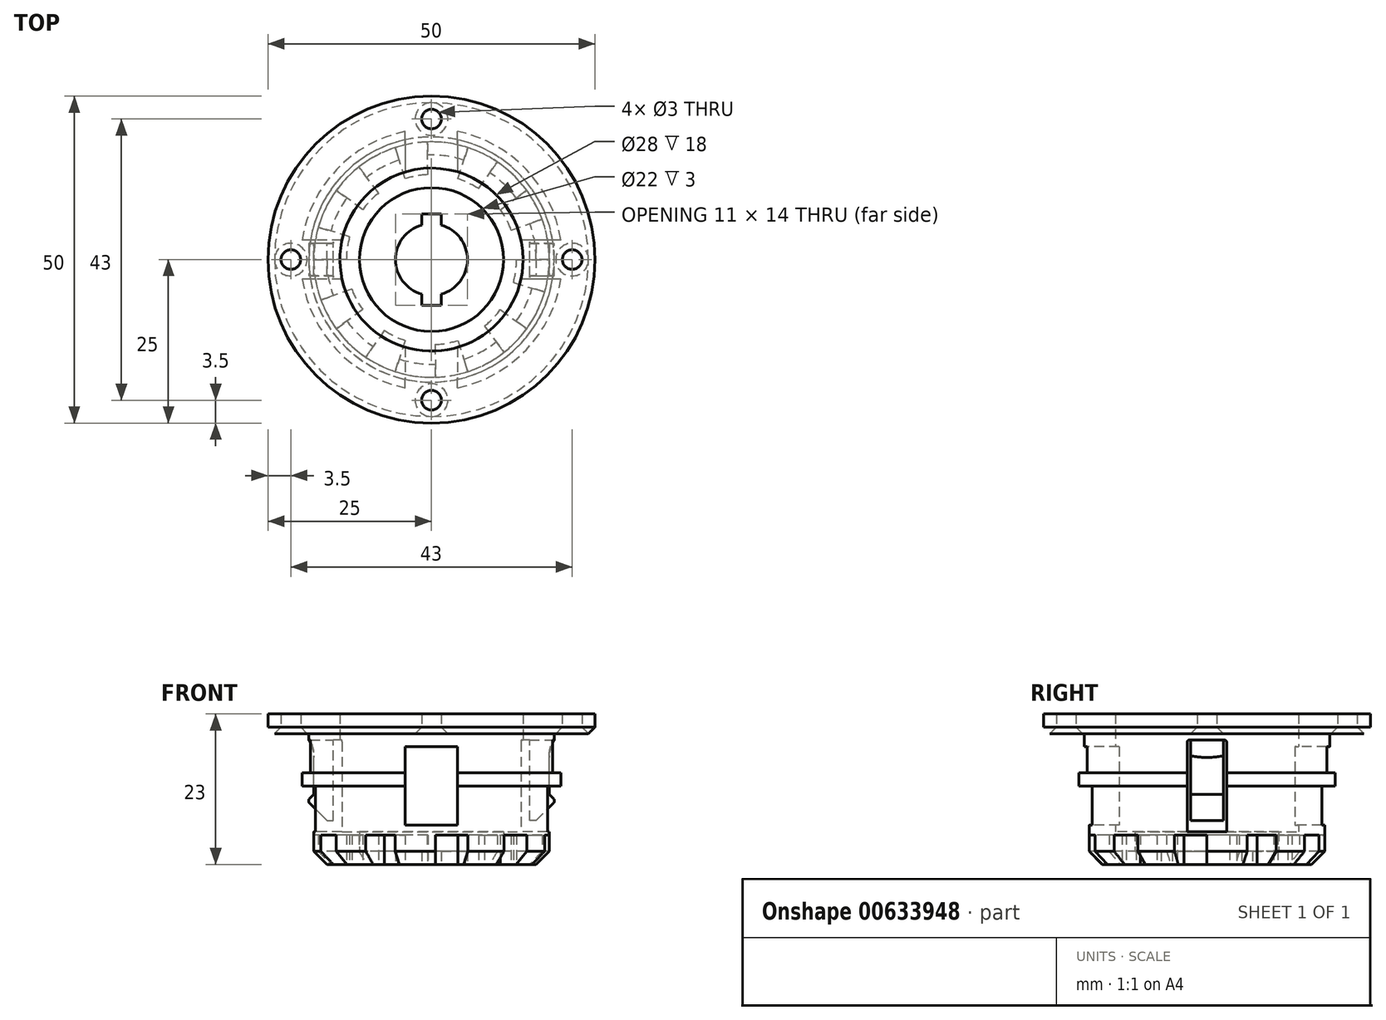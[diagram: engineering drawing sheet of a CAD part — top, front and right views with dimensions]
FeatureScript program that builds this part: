
annotation { "Feature Type Name" : "Feature", "Feature Type Description" : "" }
export const myFeature = defineFeature(function(context is Context, id is Id, definition is map)
    precondition{}
    {
        {
            var Q0;
            Q0=qCreatedBy(makeId("Top.planeOp"),FACE);
            var sketch = newSketch(context, id + "F0", { "sketchPlane" : qUnion([Q0])});
            skArc(sketch, "E0", {"start": v(18, 0) * mm, "mid": v(17.83, -2.5) * mm, "end": v(17.3, -4.95) * mm});
            skArc(sketch, "E1", {"start": v(13, 0) * mm, "mid": v(12.88, -1.77) * mm, "end": v(12.52, -3.5) * mm});
            skLineSegment(sketch, "E2", {"start": v(13, 0) * mm, "end": v(18, 0) * mm});
            skLineSegment(sketch, "E3", {"start": v(12.52, -3.5) * mm, "end": v(17.3, -4.95) * mm});
            skArc(sketch, "E4.1.0", {"start": v(10.52, -7.64) * mm, "mid": v(9.38, -9) * mm, "end": v(8.07, -10.2) * mm});
            skArc(sketch, "E4.1.1", {"start": v(14.56, -10.58) * mm, "mid": v(12.95, -12.5) * mm, "end": v(11.1, -14.18) * mm});
            skLineSegment(sketch, "E4.1.2", {"start": v(10.52, -7.64) * mm, "end": v(14.56, -10.58) * mm});
            skLineSegment(sketch, "E4.1.3", {"start": v(8.07, -10.2) * mm, "end": v(11.1, -14.18) * mm});
            skArc(sketch, "E4.2.0", {"start": v(4.02, -12.36) * mm, "mid": v(2.3, -12.8) * mm, "end": v(0.54, -12.99) * mm});
            skArc(sketch, "E4.2.1", {"start": v(5.56, -17.12) * mm, "mid": v(3.13, -17.73) * mm, "end": v(0.64, -17.99) * mm});
            skLineSegment(sketch, "E4.2.2", {"start": v(4.02, -12.36) * mm, "end": v(5.56, -17.12) * mm});
            skLineSegment(sketch, "E4.2.3", {"start": v(0.54, -12.99) * mm, "end": v(0.64, -17.99) * mm});
            skArc(sketch, "E4.3.0", {"start": v(-4.02, -12.36) * mm, "mid": v(-5.66, -11.7) * mm, "end": v(-7.2, -10.83) * mm});
            skArc(sketch, "E4.3.1", {"start": v(-5.56, -17.12) * mm, "mid": v(-7.89, -16.18) * mm, "end": v(-10.06, -14.93) * mm});
            skLineSegment(sketch, "E4.3.2", {"start": v(-4.02, -12.36) * mm, "end": v(-5.56, -17.12) * mm});
            skLineSegment(sketch, "E4.3.3", {"start": v(-7.2, -10.83) * mm, "end": v(-10.06, -14.93) * mm});
            skArc(sketch, "E4.4.0", {"start": v(-10.52, -7.64) * mm, "mid": v(-11.46, -6.14) * mm, "end": v(-12.19, -4.53) * mm});
            skArc(sketch, "E4.4.1", {"start": v(-14.56, -10.58) * mm, "mid": v(-15.9, -8.46) * mm, "end": v(-16.91, -6.17) * mm});
            skLineSegment(sketch, "E4.4.2", {"start": v(-10.52, -7.64) * mm, "end": v(-14.56, -10.58) * mm});
            skLineSegment(sketch, "E4.4.3", {"start": v(-12.19, -4.53) * mm, "end": v(-16.91, -6.17) * mm});
            skArc(sketch, "E4.5.0", {"start": v(-13, 0) * mm, "mid": v(-12.88, 1.77) * mm, "end": v(-12.52, 3.5) * mm});
            skArc(sketch, "E4.5.1", {"start": v(-18, 0) * mm, "mid": v(-17.83, 2.5) * mm, "end": v(-17.3, 4.95) * mm});
            skLineSegment(sketch, "E4.5.2", {"start": v(-13, 0) * mm, "end": v(-18, 0) * mm});
            skLineSegment(sketch, "E4.5.3", {"start": v(-12.52, 3.5) * mm, "end": v(-17.3, 4.95) * mm});
            skArc(sketch, "E4.6.0", {"start": v(-10.52, 7.64) * mm, "mid": v(-9.38, 9) * mm, "end": v(-8.07, 10.2) * mm});
            skArc(sketch, "E4.6.1", {"start": v(-14.56, 10.58) * mm, "mid": v(-12.95, 12.5) * mm, "end": v(-11.1, 14.18) * mm});
            skLineSegment(sketch, "E4.6.2", {"start": v(-10.52, 7.64) * mm, "end": v(-14.56, 10.58) * mm});
            skLineSegment(sketch, "E4.6.3", {"start": v(-8.07, 10.2) * mm, "end": v(-11.1, 14.18) * mm});
            skArc(sketch, "E4.7.0", {"start": v(-4.02, 12.36) * mm, "mid": v(-2.3, 12.8) * mm, "end": v(-0.54, 12.99) * mm});
            skArc(sketch, "E4.7.1", {"start": v(-5.56, 17.12) * mm, "mid": v(-3.13, 17.73) * mm, "end": v(-0.64, 17.99) * mm});
            skLineSegment(sketch, "E4.7.2", {"start": v(-4.02, 12.36) * mm, "end": v(-5.56, 17.12) * mm});
            skLineSegment(sketch, "E4.7.3", {"start": v(-0.54, 12.99) * mm, "end": v(-0.64, 17.99) * mm});
            skArc(sketch, "E4.8.0", {"start": v(4.02, 12.36) * mm, "mid": v(5.66, 11.7) * mm, "end": v(7.2, 10.83) * mm});
            skArc(sketch, "E4.8.1", {"start": v(5.56, 17.12) * mm, "mid": v(7.89, 16.18) * mm, "end": v(10.06, 14.93) * mm});
            skLineSegment(sketch, "E4.8.2", {"start": v(4.02, 12.36) * mm, "end": v(5.56, 17.12) * mm});
            skLineSegment(sketch, "E4.8.3", {"start": v(7.2, 10.83) * mm, "end": v(10.06, 14.93) * mm});
            skArc(sketch, "E4.9.0", {"start": v(10.52, 7.64) * mm, "mid": v(11.46, 6.14) * mm, "end": v(12.19, 4.53) * mm});
            skArc(sketch, "E4.9.1", {"start": v(14.56, 10.58) * mm, "mid": v(15.9, 8.46) * mm, "end": v(16.91, 6.17) * mm});
            skLineSegment(sketch, "E4.9.2", {"start": v(10.52, 7.64) * mm, "end": v(14.56, 10.58) * mm});
            skLineSegment(sketch, "E4.9.3", {"start": v(12.19, 4.53) * mm, "end": v(16.91, 6.17) * mm});
            skLineSegment(sketch, "E4.anchor1", {"start": v(0, 0) * mm, "end": v(12.52, -3.5) * mm, "construction": true});
            skLineSegment(sketch, "E4.anchor2", {"start": v(0, 0) * mm, "end": v(12.19, 4.53) * mm, "construction": true});
            skSolve(sketch);
        }
        {
            var Q0;
            Q0=qCreatedBy(makeId("Top.planeOp"),FACE);
            var sketch = newSketch(context, id + "F1", { "sketchPlane" : qUnion([Q0])});
            skCircle(sketch, "E5", {"center": v(0, 0) * mm, "radius": 18 * mm});
            skSolve(sketch);
        }
        {
            var Q0;
            Q0 = qSketchRegion(id + "F1", true);
            extrude(context, id + "F2", {"entities" : qUnion([Q0]), "depth" : 20 * mm, "offsetDistance" : 25 * mm});
        }
        {
            var Q0;
            Q0 = qSketchRegion(id + "F0", true);
            extrude(context, id + "F3", {"entities" : qUnion([Q0]), "operationType" : NewBodyOperationType.REMOVE, "depth" : 4.5 * mm, "offsetDistance" : 25 * mm});
        }
        {
            var Q0;
            Q0=qCreatedBy(makeId("Top.planeOp"),FACE);
            var sketch = newSketch(context, id + "F4", { "sketchPlane" : qUnion([Q0])});
            skCircle(sketch, "E6", {"center": v(0, 0) * mm, "radius": 5.5 * mm});
            skSolve(sketch);
        }
        {
            var Q0;
            Q0 = qSketchRegion(id + "F4", true);
            extrude(context, id + "F5", {"entities" : qUnion([Q0]), "operationType" : NewBodyOperationType.REMOVE, "depth" : 40 * mm, "offsetDistance" : 25 * mm});
        }
        {
            var Q0;
            Q0=qCreatedBy(makeId("Top.planeOp"),FACE);
            var sketch = newSketch(context, id + "F6", { "sketchPlane" : qUnion([Q0])});
            skCircle(sketch, "E7", {"center": v(0, 0) * mm, "radius": 14 * mm});
            skCircle(sketch, "E8", {"center": v(0, 0) * mm, "radius": 5.5 * mm});
            skSolve(sketch);
        }
        {
            var Q0;
            Q0 = qSketchRegion(id + "F6", true);
            extrude(context, id + "F7", {"entities" : qUnion([Q0]), "operationType" : NewBodyOperationType.REMOVE, "depth" : 40 * mm, "offsetDistance" : 25 * mm, "hasSecondDirection" : true, "secondDirectionOppositeDirection" : false, "secondDirectionDepth" : 5 * mm});
        }
        {
            var Q0;
            Q0=qCreatedBy(makeId("Top.planeOp"),FACE);
            var sketch = newSketch(context, id + "F8", { "sketchPlane" : qUnion([Q0])});
            skCircle(sketch, "E9", {"center": v(0, 0) * mm, "radius": 5.5 * mm});
            skCircle(sketch, "E10", {"center": v(0, 0) * mm, "radius": 11 * mm});
            skSolve(sketch);
        }
        {
            var Q0;
            Q0 = qSketchRegion(id + "F8", true);
            extrude(context, id + "F9", {"entities" : qUnion([Q0]), "operationType" : NewBodyOperationType.REMOVE, "depth" : 5 * mm, "offsetDistance" : 25 * mm, "hasSecondDirection" : true, "secondDirectionOppositeDirection" : false, "secondDirectionDepth" : 2 * mm});
        }
        {
            var Q0;
            Q0=qCreatedBy(makeId("Top.planeOp"),FACE);
            var sketch = newSketch(context, id + "F10", { "sketchPlane" : qUnion([Q0])});
            skCircle(sketch, "E11", {"center": v(0, 0) * mm, "radius": 25 * mm});
            skCircle(sketch, "E12", {"center": v(0, 0) * mm, "radius": 14 * mm});
            skSolve(sketch);
        }
        {
            var Q0;
            Q0 = qSketchRegion(id + "F10", true);
            extrude(context, id + "F11", {"entities" : qUnion([Q0]), "operationType" : NewBodyOperationType.ADD, "depth" : 23 * mm, "offsetDistance" : 25 * mm, "hasSecondDirection" : true, "secondDirectionOppositeDirection" : false, "secondDirectionDepth" : 20 * mm});
        }
        {
            var Q0;
            Q0=qCreatedBy(makeId("Top.planeOp"),FACE);
            var sketch = newSketch(context, id + "F12", { "sketchPlane" : qUnion([Q0])});
            skCircle(sketch, "E13", {"center": v(0, 0) * mm, "radius": 20 * mm});
            skCircle(sketch, "E14", {"center": v(0, 0) * mm, "radius": 18 * mm});
            skSolve(sketch);
        }
        {
            var Q0;
            Q0 = qSketchRegion(id + "F12", true);
            extrude(context, id + "F13", {"entities" : qUnion([Q0]), "operationType" : NewBodyOperationType.ADD, "depth" : 14 * mm, "offsetDistance" : 25 * mm, "hasSecondDirection" : true, "secondDirectionOppositeDirection" : false, "secondDirectionDepth" : 12 * mm});
        }
        {
            var Q0;
            Q0=qCreatedBy(makeId("Top.planeOp"),FACE);
            var sketch = newSketch(context, id + "F14", { "sketchPlane" : qUnion([Q0])});
            skCircle(sketch, "E15", {"center": v(0, 0) * mm, "radius": 18 * mm});
            skCircle(sketch, "E16", {"center": v(0, 0) * mm, "radius": 18.75 * mm});
            skSolve(sketch);
        }
        {
            var Q0;
            Q0 = qSketchRegion(id + "F14", true);
            extrude(context, id + "F15", {"entities" : qUnion([Q0]), "operationType" : NewBodyOperationType.ADD, "depth" : 20 * mm, "offsetDistance" : 25 * mm, "hasSecondDirection" : true, "secondDirectionOppositeDirection" : false, "secondDirectionDepth" : 14 * mm});
        }
        {
            var Q0;
            Q0=qCreatedBy(makeId("Top.planeOp"),FACE);
            var sketch = newSketch(context, id + "F16", { "sketchPlane" : qUnion([Q0])});
            skCircle(sketch, "E17", {"center": v(21.5, 0) * mm, "radius": 1.5 * mm});
            skCircle(sketch, "E18.1.0", {"center": v(0, 21.5) * mm, "radius": 1.5 * mm});
            skCircle(sketch, "E18.2.0", {"center": v(-21.5, 0) * mm, "radius": 1.5 * mm});
            skCircle(sketch, "E18.3.0", {"center": v(0, -21.5) * mm, "radius": 1.5 * mm});
            skPoint(sketch, "E18.center", {"position": v(0, 0) * mm});
            skSolve(sketch);
        }
        {
            var Q0;
            Q0 = qSketchRegion(id + "F16", true);
            extrude(context, id + "F17", {"entities" : qUnion([Q0]), "operationType" : NewBodyOperationType.REMOVE, "depth" : 25 * mm, "offsetDistance" : 25 * mm});
        }
        {
            var Q0;
            Q0=makeQuery(id+"F11.opExtrude","CAP_EDGE",EDGE,{"disambiguationData":[OSD([sQuery(id+"F10.wireOp",EDGE,"E11")])],"isStart":true});
            chamfer(context, id + "F18", {"entities" : qUnion([Q0]), "width" : 1 * mm, "tangentPropagation" : true});
        }
        {
            var Q0;
            {var subQ0=sQuery(id+"F1.wireOp",EDGE,"E5");Q0=makeQuery(id+"F3.boolean.opBoolean","SPLIT",EDGE,{"disambiguationData":[TD([makeQuery(id+"F3.opExtrude","SWEPT_FACE",FACE,{"disambiguationData":[OSD([sQuery(id+"F0.wireOp",EDGE,"E4.1.3")])]})])],"derivedFrom":makeQuery(id+"F2.opExtrude","CAP_EDGE",EDGE,{"disambiguationData":[OSD([subQ0])],"isStart":true})});}
            var Q1;
            {var subQ0=sQuery(id+"F1.wireOp",EDGE,"E5");Q1=makeQuery(id+"F3.boolean.opBoolean","SPLIT",EDGE,{"disambiguationData":[TD([makeQuery(id+"F3.opExtrude","SWEPT_FACE",FACE,{"disambiguationData":[OSD([sQuery(id+"F0.wireOp",EDGE,"E4.2.3")])]})])],"derivedFrom":makeQuery(id+"F2.opExtrude","CAP_EDGE",EDGE,{"disambiguationData":[OSD([subQ0])],"isStart":true})});}
            var Q2;
            {var subQ0=sQuery(id+"F1.wireOp",EDGE,"E5");Q2=makeQuery(id+"F3.boolean.opBoolean","SPLIT",EDGE,{"disambiguationData":[TD([makeQuery(id+"F3.opExtrude","SWEPT_FACE",FACE,{"disambiguationData":[OSD([sQuery(id+"F0.wireOp",EDGE,"E4.3.3")])]})])],"derivedFrom":makeQuery(id+"F2.opExtrude","CAP_EDGE",EDGE,{"disambiguationData":[OSD([subQ0])],"isStart":true})});}
            var Q3;
            {var subQ0=sQuery(id+"F1.wireOp",EDGE,"E5");Q3=makeQuery(id+"F3.boolean.opBoolean","SPLIT",EDGE,{"disambiguationData":[TD([makeQuery(id+"F3.opExtrude","SWEPT_FACE",FACE,{"disambiguationData":[OSD([sQuery(id+"F0.wireOp",EDGE,"E4.4.3")])]})])],"derivedFrom":makeQuery(id+"F2.opExtrude","CAP_EDGE",EDGE,{"disambiguationData":[OSD([subQ0])],"isStart":true})});}
            var Q4;
            {var subQ0=sQuery(id+"F1.wireOp",EDGE,"E5");Q4=makeQuery(id+"F3.boolean.opBoolean","SPLIT",EDGE,{"disambiguationData":[TD([makeQuery(id+"F3.opExtrude","SWEPT_FACE",FACE,{"disambiguationData":[OSD([sQuery(id+"F0.wireOp",EDGE,"E4.5.3")])]})])],"derivedFrom":makeQuery(id+"F2.opExtrude","CAP_EDGE",EDGE,{"disambiguationData":[OSD([subQ0])],"isStart":true})});}
            var Q5;
            {var subQ0=sQuery(id+"F1.wireOp",EDGE,"E5");Q5=makeQuery(id+"F3.boolean.opBoolean","SPLIT",EDGE,{"disambiguationData":[TD([makeQuery(id+"F3.opExtrude","SWEPT_FACE",FACE,{"disambiguationData":[OSD([sQuery(id+"F0.wireOp",EDGE,"E4.6.3")])]})])],"derivedFrom":makeQuery(id+"F2.opExtrude","CAP_EDGE",EDGE,{"disambiguationData":[OSD([subQ0])],"isStart":true})});}
            var Q6;
            {var subQ0=sQuery(id+"F1.wireOp",EDGE,"E5");Q6=makeQuery(id+"F3.boolean.opBoolean","SPLIT",EDGE,{"disambiguationData":[TD([makeQuery(id+"F3.opExtrude","SWEPT_FACE",FACE,{"disambiguationData":[OSD([sQuery(id+"F0.wireOp",EDGE,"E4.7.3")])]})])],"derivedFrom":makeQuery(id+"F2.opExtrude","CAP_EDGE",EDGE,{"disambiguationData":[OSD([subQ0])],"isStart":true})});}
            var Q7;
            {var subQ0=sQuery(id+"F1.wireOp",EDGE,"E5");Q7=makeQuery(id+"F3.boolean.opBoolean","SPLIT",EDGE,{"disambiguationData":[TD([makeQuery(id+"F3.opExtrude","SWEPT_FACE",FACE,{"disambiguationData":[OSD([sQuery(id+"F0.wireOp",EDGE,"E4.8.3")])]})])],"derivedFrom":makeQuery(id+"F2.opExtrude","CAP_EDGE",EDGE,{"disambiguationData":[OSD([subQ0])],"isStart":true})});}
            var Q8;
            {var subQ0=sQuery(id+"F1.wireOp",EDGE,"E5");Q8=makeQuery(id+"F3.boolean.opBoolean","SPLIT",EDGE,{"disambiguationData":[TD([makeQuery(id+"F3.opExtrude","SWEPT_FACE",FACE,{"disambiguationData":[OSD([sQuery(id+"F0.wireOp",EDGE,"E2")])]})])],"derivedFrom":makeQuery(id+"F2.opExtrude","CAP_EDGE",EDGE,{"disambiguationData":[OSD([subQ0])],"isStart":true})});}
            var Q9;
            {var subQ0=sQuery(id+"F1.wireOp",EDGE,"E5");Q9=makeQuery(id+"F3.boolean.opBoolean","SPLIT",EDGE,{"disambiguationData":[TD([makeQuery(id+"F3.opExtrude","SWEPT_FACE",FACE,{"disambiguationData":[OSD([sQuery(id+"F0.wireOp",EDGE,"E3")])]})])],"derivedFrom":makeQuery(id+"F2.opExtrude","CAP_EDGE",EDGE,{"disambiguationData":[OSD([subQ0])],"isStart":true})});}
            chamfer(context, id + "F19", {"entities" : qUnion([Q0, Q1, Q2, Q3, Q4, Q5, Q6, Q7, Q8, Q9]), "width" : 2 * mm, "tangentPropagation" : true});
        }
        {
            var Q0;
            Q0=qCreatedBy(makeId("Right.planeOp"),FACE);
            var sketch = newSketch(context, id + "F20", { "sketchPlane" : qUnion([Q0])});
            skLineSegment(sketch, "E19.bottom", {"start": v(-3, 19) * mm, "end": v(3, 19) * mm});
            skLineSegment(sketch, "E19.top", {"start": v(-3, 5) * mm, "end": v(3, 5) * mm});
            skLineSegment(sketch, "E19.left", {"start": v(-3, 19) * mm, "end": v(-3, 5) * mm});
            skLineSegment(sketch, "E19.right", {"start": v(3, 19) * mm, "end": v(3, 5) * mm});
            skPoint(sketch, "E19.middle", {"position": v(0, 12) * mm});
            skSolve(sketch);
        }
        {
            var Q0;
            Q0 = qSketchRegion(id + "F20", true);
            extrude(context, id + "F21", {"entities" : qUnion([Q0]), "operationType" : NewBodyOperationType.REMOVE, "endBound" : BoundingType.SYMMETRIC, "depth" : 40 * mm, "offsetDistance" : 25 * mm});
        }
        {
            var Q0;
            Q0=qCreatedBy(makeId("Right.planeOp"),FACE);
            var sketch = newSketch(context, id + "F22", { "sketchPlane" : qUnion([Q0])});
            skLineSegment(sketch, "E20.bottom", {"start": v(-2.5, 6.7) * mm, "end": v(2.5, 6.7) * mm});
            skLineSegment(sketch, "E20.top", {"start": v(-2.5, 19.7) * mm, "end": v(2.5, 19.7) * mm});
            skLineSegment(sketch, "E20.left", {"start": v(-2.5, 6.7) * mm, "end": v(-2.5, 19.7) * mm});
            skLineSegment(sketch, "E20.right", {"start": v(2.5, 6.7) * mm, "end": v(2.5, 19.7) * mm});
            skSolve(sketch);
        }
        {
            var Q0;
            Q0 = qSketchRegion(id + "F22", true);
            extrude(context, id + "F23", {"entities" : qUnion([Q0]), "operationType" : NewBodyOperationType.ADD, "depth" : 18 * mm, "offsetDistance" : 25 * mm, "hasSecondDirection" : true, "secondDirectionOppositeDirection" : false, "secondDirectionDepth" : 15 * mm});
        }
        {
            var Q0;
            Q0 = qSketchRegion(id + "F22", true);
            extrude(context, id + "F24", {"entities" : qUnion([Q0]), "operationType" : NewBodyOperationType.ADD, "oppositeDirection" : true, "depth" : 18 * mm, "offsetDistance" : 25 * mm, "hasSecondDirection" : true, "secondDirectionOppositeDirection" : true, "secondDirectionDepth" : 15 * mm});
        }
        {
            var Q0;
            Q0=qCreatedBy(makeId("Right.planeOp"),FACE);
            var sketch = newSketch(context, id + "F25", { "sketchPlane" : qUnion([Q0])});
            skLineSegment(sketch, "E21.bottom", {"start": v(2.5, 6.7) * mm, "end": v(-2.5, 6.7) * mm});
            skLineSegment(sketch, "E21.top", {"start": v(2.5, 12.7) * mm, "end": v(-2.5, 12.7) * mm});
            skLineSegment(sketch, "E21.left", {"start": v(2.5, 6.7) * mm, "end": v(2.5, 12.7) * mm});
            skLineSegment(sketch, "E21.right", {"start": v(-2.5, 6.7) * mm, "end": v(-2.5, 12.7) * mm});
            skPoint(sketch, "E21.middle", {"position": v(0, 9.7) * mm});
            skSolve(sketch);
        }
        {
            var Q0;
            Q0 = qSketchRegion(id + "F25", true);
            extrude(context, id + "F26", {"entities" : qUnion([Q0]), "operationType" : NewBodyOperationType.ADD, "depth" : 19 * mm, "offsetDistance" : 25 * mm, "hasSecondDirection" : true, "secondDirectionOppositeDirection" : false, "secondDirectionDepth" : 18 * mm});
        }
        {
            var Q0;
            Q0 = qSketchRegion(id + "F25", true);
            extrude(context, id + "F27", {"entities" : qUnion([Q0]), "operationType" : NewBodyOperationType.ADD, "oppositeDirection" : true, "depth" : 19 * mm, "offsetDistance" : 25 * mm, "hasSecondDirection" : true, "secondDirectionOppositeDirection" : true, "secondDirectionDepth" : 18 * mm});
        }
        {
            var Q0;
            Q0=makeQuery(id+"F27.opExtrude","CAP_EDGE",EDGE,{"disambiguationData":[OSD([sQuery(id+"F25.wireOp",EDGE,"E21.top")])],"isStart":false});
            var Q1;
            Q1=makeQuery(id+"F27.opExtrude","CAP_EDGE",EDGE,{"disambiguationData":[OSD([sQuery(id+"F25.wireOp",EDGE,"E21.bottom")])],"isStart":false});
            var Q2;
            Q2=makeQuery(id+"F26.opExtrude","CAP_EDGE",EDGE,{"disambiguationData":[OSD([sQuery(id+"F25.wireOp",EDGE,"E21.bottom")])],"isStart":false});
            var Q3;
            Q3=makeQuery(id+"F26.opExtrude","CAP_EDGE",EDGE,{"disambiguationData":[OSD([sQuery(id+"F25.wireOp",EDGE,"E21.top")])],"isStart":false});
            chamfer(context, id + "F28", {"entities" : qUnion([Q0, Q1, Q2, Q3]), "width" : 3 * mm, "tangentPropagation" : true});
        }
        {
            var Q0;
            Q0=makeQuery(id+"F28.opChamfer","BLEND_EDGE",EDGE,{"blendedFrom":[makeQuery(id+"F26.opExtrude","CAP_EDGE",EDGE,{"disambiguationData":[OSD([sQuery(id+"F25.wireOp",EDGE,"E21.bottom")])],"isStart":false}),makeQuery(id+"F26.opExtrude","CAP_EDGE",EDGE,{"disambiguationData":[OSD([sQuery(id+"F25.wireOp",EDGE,"E21.top")])],"isStart":false})],"blendedInto":[]});
            var Q1;
            Q1=makeQuery(id+"F28.opChamfer","BLEND_EDGE",EDGE,{"blendedFrom":[makeQuery(id+"F27.opExtrude","CAP_EDGE",EDGE,{"disambiguationData":[OSD([sQuery(id+"F25.wireOp",EDGE,"E21.bottom")])],"isStart":false}),makeQuery(id+"F27.opExtrude","CAP_EDGE",EDGE,{"disambiguationData":[OSD([sQuery(id+"F25.wireOp",EDGE,"E21.top")])],"isStart":false})],"blendedInto":[]});
            fillet(context, id + "F29", {"entities" : qUnion([Q0, Q1]), "radius" : 0.5 * mm, "tangentPropagation" : true, "allowEdgeOverflow" : false});
        }
        {
            var Q0;
            Q0=makeQuery(id+"F23.boolean.opBoolean","INTERSECT",EDGE,{"derivedFrom":[makeQuery(id+"F21.boolean.opBoolean","COPY",FACE,{"disambiguationData":[OD(1.0)],"derivedFrom":makeQuery(id+"F21.opExtrude","SWEPT_FACE",FACE,{"disambiguationData":[OSD([sQuery(id+"F20.wireOp",EDGE,"E19.bottom")])]})}),makeQuery(id+"F23.opExtrude","CAP_FACE",FACE,{"disambiguationData":[OSD([sQuery(id+"F22.wireOp",EDGE,"E20.bottom"),sQuery(id+"F22.wireOp",EDGE,"E20.top"),sQuery(id+"F22.wireOp",EDGE,"E20.left"),sQuery(id+"F22.wireOp",EDGE,"E20.right")])],"isStart":false})]});
            var Q1;
            Q1=makeQuery(id+"F24.boolean.opBoolean","INTERSECT",EDGE,{"derivedFrom":[makeQuery(id+"F21.boolean.opBoolean","COPY",FACE,{"disambiguationData":[OD(0.0)],"derivedFrom":makeQuery(id+"F21.opExtrude","SWEPT_FACE",FACE,{"disambiguationData":[OSD([sQuery(id+"F20.wireOp",EDGE,"E19.bottom")])]})}),makeQuery(id+"F24.opExtrude","CAP_FACE",FACE,{"disambiguationData":[OSD([sQuery(id+"F22.wireOp",EDGE,"E20.bottom"),sQuery(id+"F22.wireOp",EDGE,"E20.top"),sQuery(id+"F22.wireOp",EDGE,"E20.left"),sQuery(id+"F22.wireOp",EDGE,"E20.right")])],"isStart":false})]});
            fillet(context, id + "F30", {"entities" : qUnion([Q0, Q1]), "radius" : 5 * mm, "tangentPropagation" : true, "allowEdgeOverflow" : false});
        }
        {
            var Q0;
            Q0=makeQuery(id+"F24.boolean.opBoolean","INTERSECT",EDGE,{"derivedFrom":[makeQuery(id+"F21.boolean.opBoolean","COPY",FACE,{"disambiguationData":[OD(0.0)],"derivedFrom":makeQuery(id+"F21.opExtrude","SWEPT_FACE",FACE,{"disambiguationData":[OSD([sQuery(id+"F20.wireOp",EDGE,"E19.bottom")])]})}),makeQuery(id+"F24.opExtrude","SWEPT_FACE",FACE,{"disambiguationData":[OSD([sQuery(id+"F22.wireOp",EDGE,"E20.left")])]})]});
            var Q1;
            Q1=makeQuery(id+"F21.boolean.opBoolean","COPY",EDGE,{"disambiguationData":[OD(0.0)],"derivedFrom":makeQuery(id+"F21.opExtrude","SWEPT_EDGE",EDGE,{"disambiguationData":[OSD([sQuery(id+"F20.wireOp",EDGE,"E19.bottom"),sQuery(id+"F20.wireOp",EDGE,"E19.left")])]})});
            var Q2;
            Q2=makeQuery(id+"F21.boolean.opBoolean","COPY",EDGE,{"disambiguationData":[OD(0.0)],"derivedFrom":makeQuery(id+"F21.opExtrude","SWEPT_EDGE",EDGE,{"disambiguationData":[OSD([sQuery(id+"F20.wireOp",EDGE,"E19.bottom"),sQuery(id+"F20.wireOp",EDGE,"E19.right")])]})});
            var Q3;
            Q3=makeQuery(id+"F24.boolean.opBoolean","INTERSECT",EDGE,{"derivedFrom":[makeQuery(id+"F21.boolean.opBoolean","COPY",FACE,{"disambiguationData":[OD(0.0)],"derivedFrom":makeQuery(id+"F21.opExtrude","SWEPT_FACE",FACE,{"disambiguationData":[OSD([sQuery(id+"F20.wireOp",EDGE,"E19.bottom")])]})}),makeQuery(id+"F24.opExtrude","SWEPT_FACE",FACE,{"disambiguationData":[OSD([sQuery(id+"F22.wireOp",EDGE,"E20.right")])]})]});
            var Q4;
            Q4=makeQuery(id+"F21.boolean.opBoolean","COPY",EDGE,{"disambiguationData":[OD(1.0)],"derivedFrom":makeQuery(id+"F21.opExtrude","SWEPT_EDGE",EDGE,{"disambiguationData":[OSD([sQuery(id+"F20.wireOp",EDGE,"E19.bottom"),sQuery(id+"F20.wireOp",EDGE,"E19.right")])]})});
            var Q5;
            Q5=makeQuery(id+"F23.boolean.opBoolean","INTERSECT",EDGE,{"derivedFrom":[makeQuery(id+"F21.boolean.opBoolean","COPY",FACE,{"disambiguationData":[OD(1.0)],"derivedFrom":makeQuery(id+"F21.opExtrude","SWEPT_FACE",FACE,{"disambiguationData":[OSD([sQuery(id+"F20.wireOp",EDGE,"E19.bottom")])]})}),makeQuery(id+"F23.opExtrude","SWEPT_FACE",FACE,{"disambiguationData":[OSD([sQuery(id+"F22.wireOp",EDGE,"E20.left")])]})]});
            var Q6;
            Q6=makeQuery(id+"F21.boolean.opBoolean","COPY",EDGE,{"disambiguationData":[OD(1.0)],"derivedFrom":makeQuery(id+"F21.opExtrude","SWEPT_EDGE",EDGE,{"disambiguationData":[OSD([sQuery(id+"F20.wireOp",EDGE,"E19.bottom"),sQuery(id+"F20.wireOp",EDGE,"E19.left")])]})});
            var Q7;
            Q7=makeQuery(id+"F23.boolean.opBoolean","INTERSECT",EDGE,{"derivedFrom":[makeQuery(id+"F21.boolean.opBoolean","COPY",FACE,{"disambiguationData":[OD(1.0)],"derivedFrom":makeQuery(id+"F21.opExtrude","SWEPT_FACE",FACE,{"disambiguationData":[OSD([sQuery(id+"F20.wireOp",EDGE,"E19.bottom")])]})}),makeQuery(id+"F23.opExtrude","SWEPT_FACE",FACE,{"disambiguationData":[OSD([sQuery(id+"F22.wireOp",EDGE,"E20.right")])]})]});
            fillet(context, id + "F31", {"entities" : qUnion([Q0, Q1, Q2, Q3, Q4, Q5, Q6, Q7]), "radius" : 0.25 * mm, "tangentPropagation" : true, "allowEdgeOverflow" : false});
        }
        {
            var Q0;
            Q0=makeQuery(id+"F17.boolean.opBoolean","INTERSECT",EDGE,{"derivedFrom":[makeQuery(id+"F11.opExtrude","CAP_FACE",FACE,{"disambiguationData":[OSD([sQuery(id+"F10.wireOp",EDGE,"E11"),sQuery(id+"F10.wireOp",EDGE,"E12")])],"isStart":true}),makeQuery(id+"F17.opExtrude","SWEPT_FACE",FACE,{"disambiguationData":[OSD([sQuery(id+"F16.wireOp",EDGE,"E17")])]})]});
            var Q1;
            Q1=makeQuery(id+"F17.boolean.opBoolean","INTERSECT",EDGE,{"derivedFrom":[makeQuery(id+"F11.opExtrude","CAP_FACE",FACE,{"disambiguationData":[OSD([sQuery(id+"F10.wireOp",EDGE,"E11"),sQuery(id+"F10.wireOp",EDGE,"E12")])],"isStart":true}),makeQuery(id+"F17.opExtrude","SWEPT_FACE",FACE,{"disambiguationData":[OSD([sQuery(id+"F16.wireOp",EDGE,"E18.1.0")])]})]});
            var Q2;
            Q2=makeQuery(id+"F17.boolean.opBoolean","INTERSECT",EDGE,{"derivedFrom":[makeQuery(id+"F11.opExtrude","CAP_FACE",FACE,{"disambiguationData":[OSD([sQuery(id+"F10.wireOp",EDGE,"E11"),sQuery(id+"F10.wireOp",EDGE,"E12")])],"isStart":true}),makeQuery(id+"F17.opExtrude","SWEPT_FACE",FACE,{"disambiguationData":[OSD([sQuery(id+"F16.wireOp",EDGE,"E18.2.0")])]})]});
            var Q3;
            Q3=makeQuery(id+"F17.boolean.opBoolean","INTERSECT",EDGE,{"derivedFrom":[makeQuery(id+"F11.opExtrude","CAP_FACE",FACE,{"disambiguationData":[OSD([sQuery(id+"F10.wireOp",EDGE,"E11"),sQuery(id+"F10.wireOp",EDGE,"E12")])],"isStart":true}),makeQuery(id+"F17.opExtrude","SWEPT_FACE",FACE,{"disambiguationData":[OSD([sQuery(id+"F16.wireOp",EDGE,"E18.3.0")])]})]});
            chamfer(context, id + "F32", {"entities" : qUnion([Q0, Q1, Q2, Q3]), "width" : 1 * mm, "tangentPropagation" : true});
        }
        {
            var Q0;
            Q0=qCreatedBy(makeId("Top.planeOp"),FACE);
            var sketch = newSketch(context, id + "F33", { "sketchPlane" : qUnion([Q0])});
            skLineSegment(sketch, "E22.bottom", {"start": v(1.5, -7) * mm, "end": v(-1.5, -7) * mm});
            skLineSegment(sketch, "E22.top", {"start": v(1.5, -4.5) * mm, "end": v(-1.5, -4.5) * mm});
            skLineSegment(sketch, "E22.left", {"start": v(1.5, -7) * mm, "end": v(1.5, -4.5) * mm});
            skLineSegment(sketch, "E22.right", {"start": v(-1.5, -7) * mm, "end": v(-1.5, -4.5) * mm});
            skLineSegment(sketch, "E23.MirrorCS", {"start": v(1.5, 7) * mm, "end": v(-1.5, 7) * mm});
            skLineSegment(sketch, "E24.MirrorCS", {"start": v(-1.5, 7) * mm, "end": v(-1.5, 4.5) * mm});
            skLineSegment(sketch, "E25.MirrorCS", {"start": v(1.5, 7) * mm, "end": v(1.5, 4.5) * mm});
            skLineSegment(sketch, "E26.MirrorCS", {"start": v(1.5, 4.5) * mm, "end": v(-1.5, 4.5) * mm});
            skSolve(sketch);
        }
        {
            var Q0;
            Q0 = qSketchRegion(id + "F33", true);
            extrude(context, id + "F34", {"entities" : qUnion([Q0]), "operationType" : NewBodyOperationType.REMOVE, "depth" : 2 * mm, "offsetDistance" : 25 * mm, "hasSecondDirection" : true, "secondDirectionOppositeDirection" : false, "secondDirectionDepth" : 0 * mm});
        }
        {
            var Q0;
            Q0=qCreatedBy(makeId("Front.planeOp"),FACE);
            var sketch = newSketch(context, id + "F35", { "sketchPlane" : qUnion([Q0])});
            skLineSegment(sketch, "E27.bottom", {"start": v(4, 6) * mm, "end": v(-4, 6) * mm});
            skLineSegment(sketch, "E27.top", {"start": v(4, 18) * mm, "end": v(-4, 18) * mm});
            skLineSegment(sketch, "E27.left", {"start": v(4, 6) * mm, "end": v(4, 18) * mm});
            skLineSegment(sketch, "E27.right", {"start": v(-4, 6) * mm, "end": v(-4, 18) * mm});
            skPoint(sketch, "E27.middle", {"position": v(0, 12) * mm});
            skSolve(sketch);
        }
        {
            var Q0;
            Q0 = qSketchRegion(id + "F35", true);
            extrude(context, id + "F36", {"entities" : qUnion([Q0]), "operationType" : NewBodyOperationType.REMOVE, "endBound" : BoundingType.SYMMETRIC, "oppositeDirection" : true, "depth" : 40 * mm, "offsetDistance" : 25 * mm});
        }
    });
